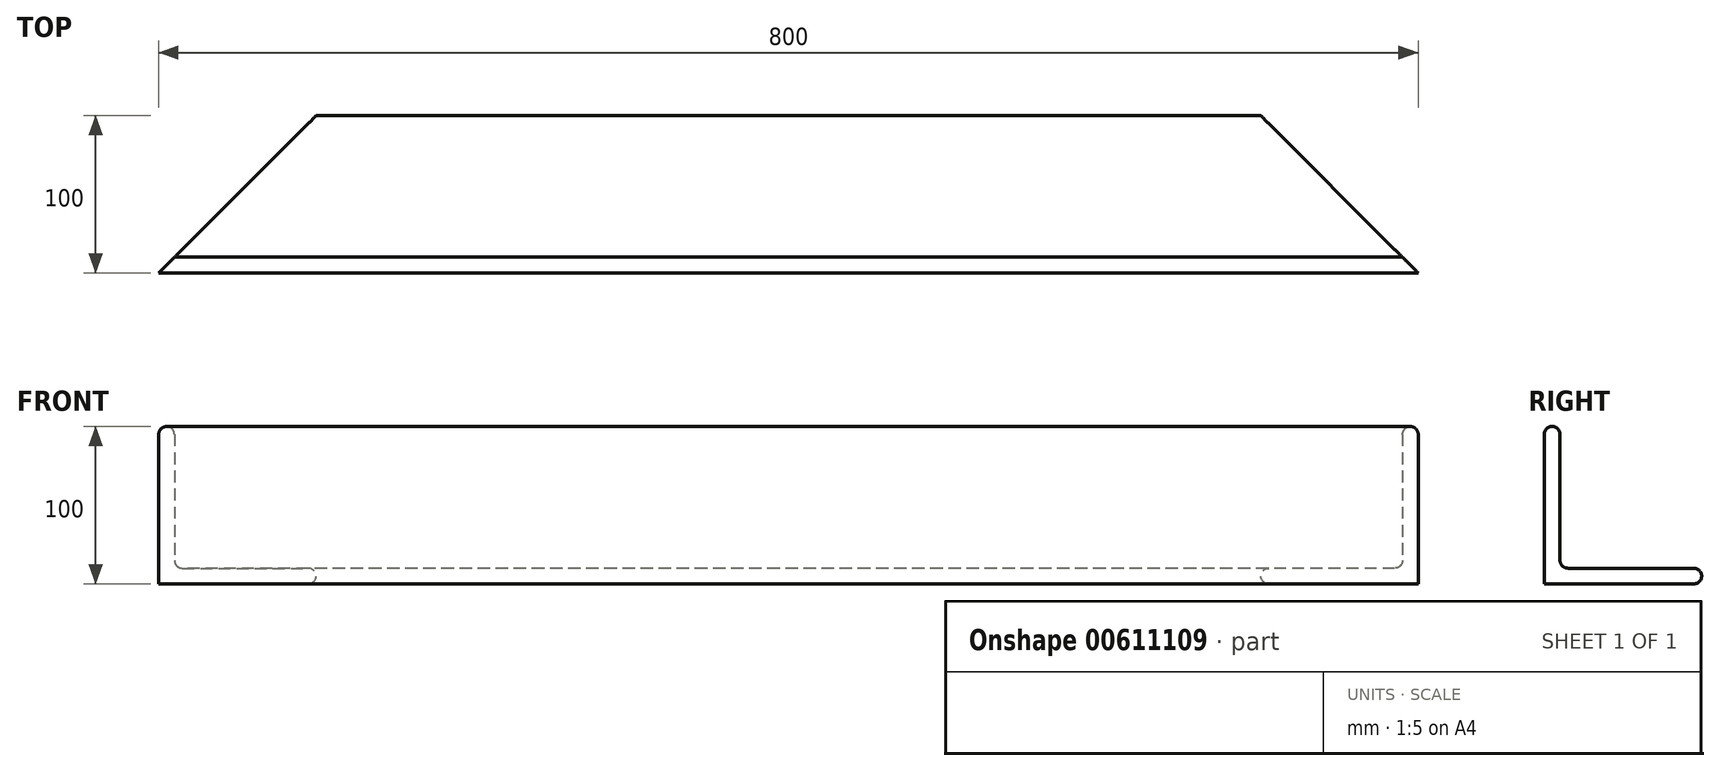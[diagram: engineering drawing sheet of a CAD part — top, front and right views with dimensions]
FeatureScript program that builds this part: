
annotation { "Feature Type Name" : "Feature", "Feature Type Description" : "" }
export const myFeature = defineFeature(function(context is Context, id is Id, definition is map)
    precondition{}
    {
        {
            var Q0;
            Q0=qCreatedBy(makeId("Right.planeOp"),FACE);
            var sketch = newSketch(context, id + "F0", { "sketchPlane" : qUnion([Q0])});
            skLineSegment(sketch, "E0", {"start": v(-12.36, 0) * mm, "end": v(-12.36, 95) * mm});
            skLineSegment(sketch, "E1", {"start": v(-7.36, 100) * mm, "end": v(-7.36, 100) * mm});
            skLineSegment(sketch, "E2", {"start": v(-2.36, 95) * mm, "end": v(-2.36, 15) * mm});
            skLineSegment(sketch, "E3", {"start": v(2.64, 10) * mm, "end": v(82.64, 10) * mm});
            skLineSegment(sketch, "E4", {"start": v(87.64, 5) * mm, "end": v(87.64, 5) * mm});
            skLineSegment(sketch, "E5", {"start": v(82.64, 0) * mm, "end": v(-12.36, 0) * mm});
            skPoint(sketch, "E6.visualSharp", {"position": v(-12.36, 100) * mm});
            skArc(sketch, "E6.filletArc", {"start": v(-7.36, 100) * mm, "mid": v(-10.9, 98.54) * mm, "end": v(-12.36, 95) * mm});
            skPoint(sketch, "E7.visualSharp", {"position": v(-2.36, 100) * mm});
            skArc(sketch, "E7.filletArc", {"start": v(-2.36, 95) * mm, "mid": v(-3.83, 98.54) * mm, "end": v(-7.36, 100) * mm});
            skPoint(sketch, "E8.visualSharp", {"position": v(-2.36, 10) * mm});
            skArc(sketch, "E8.filletArc", {"start": v(-2.36, 15) * mm, "mid": v(-0.9, 11.46) * mm, "end": v(2.64, 10) * mm});
            skPoint(sketch, "E9.visualSharp", {"position": v(87.64, 10) * mm});
            skArc(sketch, "E9.filletArc", {"start": v(87.64, 5) * mm, "mid": v(86.17, 8.54) * mm, "end": v(82.64, 10) * mm});
            skPoint(sketch, "E10.visualSharp", {"position": v(87.64, 0) * mm});
            skArc(sketch, "E10.filletArc", {"start": v(82.64, 0) * mm, "mid": v(86.17, 1.46) * mm, "end": v(87.64, 5) * mm});
            skSolve(sketch);
        }
        {
            var Q0;
            Q0=makeQuery(id+"F0.imprint","IMPRINT",FACE,{"disambiguationData":[TD([[makeQuery(id+"F0.imprint","IMPRINT",EDGE,{"derivedFrom":sQuery(id+"F0.wireOp",EDGE,"E0")}),-1.0]])]});
            extrude(context, id + "F1", {"entities" : qUnion([Q0]), "depth" : 800 * mm, "offsetDistance" : 25 * mm});
        }
        {
            var Q0;
            Q0=makeQuery(id+"F1.opExtrude","SWEPT_FACE",FACE,{"disambiguationData":[OSD([sQuery(id+"F0.wireOp",EDGE,"E5")])]});
            var sketch = newSketch(context, id + "F2", { "sketchPlane" : qUnion([Q0])});
            skLineSegment(sketch, "E11", {"start": v(800, 12.36) * mm, "end": v(800, -87.64) * mm});
            skLineSegment(sketch, "E12", {"start": v(800, -87.64) * mm, "end": v(700, -87.64) * mm});
            skLineSegment(sketch, "E13", {"start": v(700, -87.64) * mm, "end": v(800, 12.36) * mm});
            skSolve(sketch);
        }
        {
            var Q0;
            {var subQ0=sQuery(id+"F2.wireOp",EDGE,"E13");var subQ1=sQuery(id+"F2.wireOp",EDGE,"E11");var subQ2=sQuery(id+"F0.wireOp",EDGE,"E5");var subQ3=makeQuery(id+"F2.imprint","INTERSECT",VERTEX,{"derivedFrom":[makeQuery(id+"F1.opExtrude","SWEPT_EDGE",EDGE,{"disambiguationData":[OSD([sQuery(id+"F0.wireOp",EDGE,"E0"),subQ2])]}),subQ1,subQ0]});Q0=makeQuery(id+"F2.imprint","IMPRINT",FACE,{"disambiguationData":[TD([[makeQuery(id+"F2.imprint","IMPRINT",EDGE,{"disambiguationData":[TD([[subQ3,1.0]])],"derivedFrom":subQ1}),1.0]])]});}
            var Q1;
            {var subQ3=sQuery(id+"F2.wireOp",EDGE,"E12");Q1=makeQuery(id+"F2.imprint","IMPRINT",FACE,{"disambiguationData":[TD([[makeQuery(id+"F2.imprint","IMPRINT",EDGE,{"derivedFrom":subQ3}),-1.0]])]});}
            extrude(context, id + "F3", {"entities" : qUnion([Q0, Q1]), "operationType" : NewBodyOperationType.REMOVE, "oppositeDirection" : true, "depth" : 100 * mm, "offsetDistance" : 25 * mm});
        }
        {
            var Q0;
            Q0=makeQuery(id+"F1.opExtrude","SWEPT_FACE",FACE,{"disambiguationData":[OSD([sQuery(id+"F0.wireOp",EDGE,"E5")])]});
            var sketch = newSketch(context, id + "F4", { "sketchPlane" : qUnion([Q0])});
            skLineSegment(sketch, "E14", {"start": v(0, 12.36) * mm, "end": v(0, -87.64) * mm});
            skLineSegment(sketch, "E15", {"start": v(0, -87.64) * mm, "end": v(100, -87.64) * mm});
            skLineSegment(sketch, "E16", {"start": v(100, -87.64) * mm, "end": v(0, 12.36) * mm});
            skSolve(sketch);
        }
        {
            var Q0;
            {var subQ3=sQuery(id+"F4.wireOp",EDGE,"E15");Q0=makeQuery(id+"F4.imprint","IMPRINT",FACE,{"disambiguationData":[TD([[makeQuery(id+"F4.imprint","IMPRINT",EDGE,{"derivedFrom":subQ3}),1.0]])]});}
            var Q1;
            {var subQ0=sQuery(id+"F4.wireOp",EDGE,"E16");var subQ1=sQuery(id+"F4.wireOp",EDGE,"E14");var subQ2=sQuery(id+"F0.wireOp",EDGE,"E5");var subQ3=makeQuery(id+"F4.imprint","INTERSECT",VERTEX,{"derivedFrom":[makeQuery(id+"F1.opExtrude","SWEPT_EDGE",EDGE,{"disambiguationData":[OSD([sQuery(id+"F0.wireOp",EDGE,"E0"),subQ2])]}),subQ1,subQ0]});Q1=makeQuery(id+"F4.imprint","IMPRINT",FACE,{"disambiguationData":[TD([[makeQuery(id+"F4.imprint","IMPRINT",EDGE,{"disambiguationData":[TD([[subQ3,1.0]])],"derivedFrom":subQ1}),-1.0]])]});}
            extrude(context, id + "F5", {"entities" : qUnion([Q0, Q1]), "operationType" : NewBodyOperationType.REMOVE, "endBound" : BoundingType.THROUGH_ALL, "oppositeDirection" : true, "depth" : 25 * mm, "offsetDistance" : 25 * mm});
        }
    });
